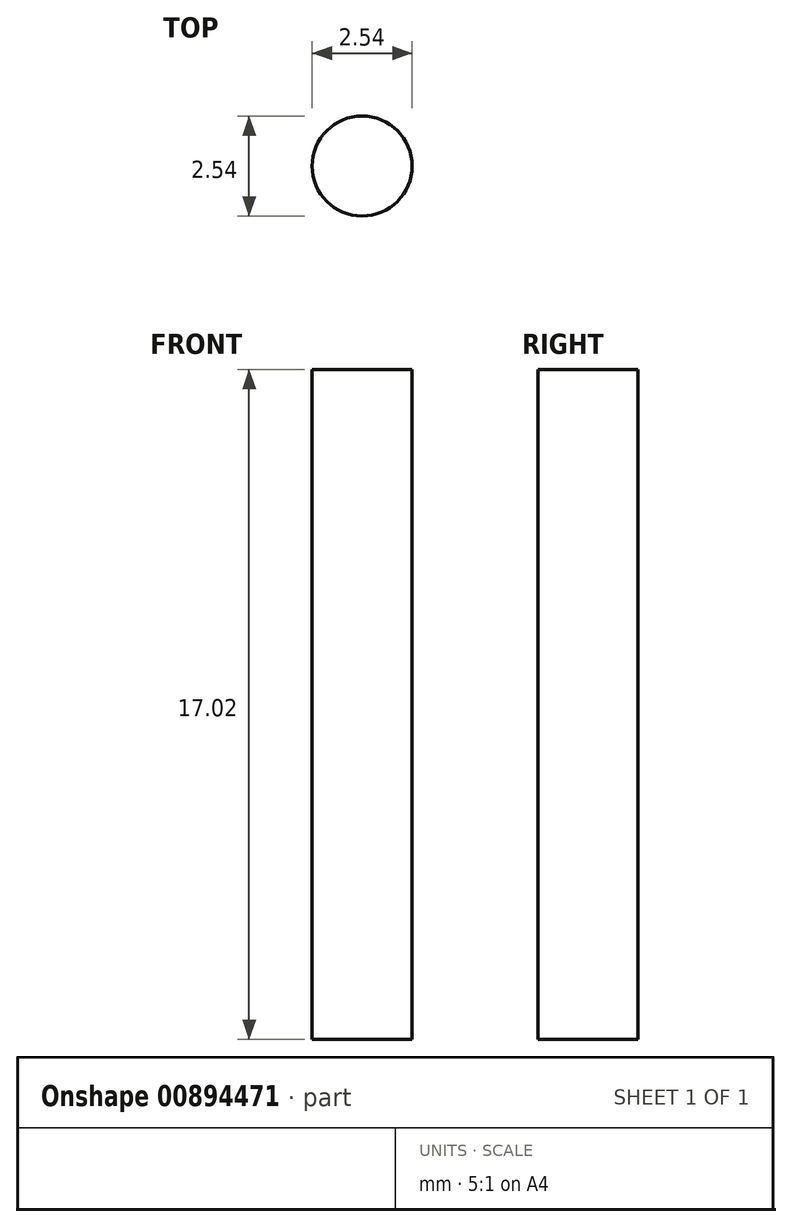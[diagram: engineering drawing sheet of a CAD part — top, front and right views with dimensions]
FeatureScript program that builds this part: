
annotation { "Feature Type Name" : "Feature", "Feature Type Description" : "" }
export const myFeature = defineFeature(function(context is Context, id is Id, definition is map)
    precondition{}
    {
        {
            var Q0;
            Q0=qCreatedBy(makeId("Top.planeOp"),FACE);
            var sketch = newSketch(context, id + "F0", { "sketchPlane" : qUnion([Q0])});
            skCircle(sketch, "E0", {"center": v(0, 0) * mm, "radius": 1.27 * mm});
            skSolve(sketch);
        }
        {
            var Q0;
            Q0=makeQuery(id+"F0.imprint","IMPRINT",FACE,{"disambiguationData":[TD([[makeQuery(id+"F0.imprint","IMPRINT",EDGE,{"derivedFrom":sQuery(id+"F0.wireOp",EDGE,"E0")}),1.0]])]});
            extrude(context, id + "F1", {"entities" : qUnion([Q0]), "depth" : 17.02 * mm, "offsetDistance" : 25.4 * mm});
        }
    });
